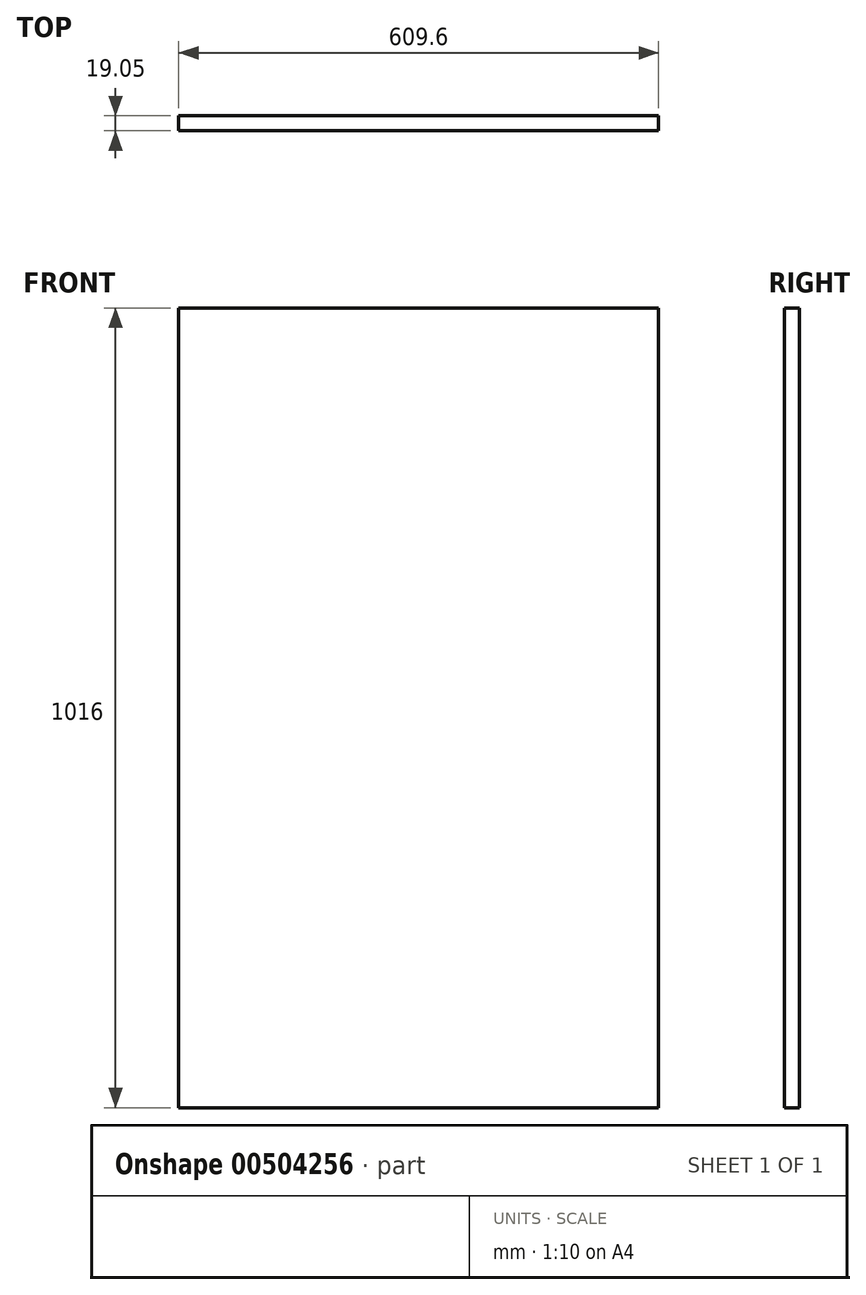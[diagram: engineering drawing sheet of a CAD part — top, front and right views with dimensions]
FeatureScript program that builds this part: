
annotation { "Feature Type Name" : "Feature", "Feature Type Description" : "" }
export const myFeature = defineFeature(function(context is Context, id is Id, definition is map)
    precondition{}
    {
        {
            var Q0;
            Q0=qCreatedBy(makeId("Front.planeOp"),FACE);
            var sketch = newSketch(context, id + "F0", { "sketchPlane" : qUnion([Q0])});
            skLineSegment(sketch, "E0.bottom", {"start": v(304.8, -508) * mm, "end": v(-304.8, -508) * mm});
            skLineSegment(sketch, "E0.top", {"start": v(304.8, 508) * mm, "end": v(-304.8, 508) * mm});
            skLineSegment(sketch, "E0.left", {"start": v(304.8, -508) * mm, "end": v(304.8, 508) * mm});
            skLineSegment(sketch, "E0.right", {"start": v(-304.8, -508) * mm, "end": v(-304.8, 508) * mm});
            skPoint(sketch, "E0.middle", {"position": v(0, 0) * mm});
            skSolve(sketch);
        }
        {
            var Q0;
            Q0=makeQuery(id+"F0.imprint","IMPRINT",FACE,{"disambiguationData":[TD([[makeQuery(id+"F0.imprint","IMPRINT",EDGE,{"derivedFrom":sQuery(id+"F0.wireOp",EDGE,"E0.bottom")}),-1.0]])]});
            extrude(context, id + "F1", {"entities" : qUnion([Q0]), "depth" : 19.05 * mm});
        }
    });
